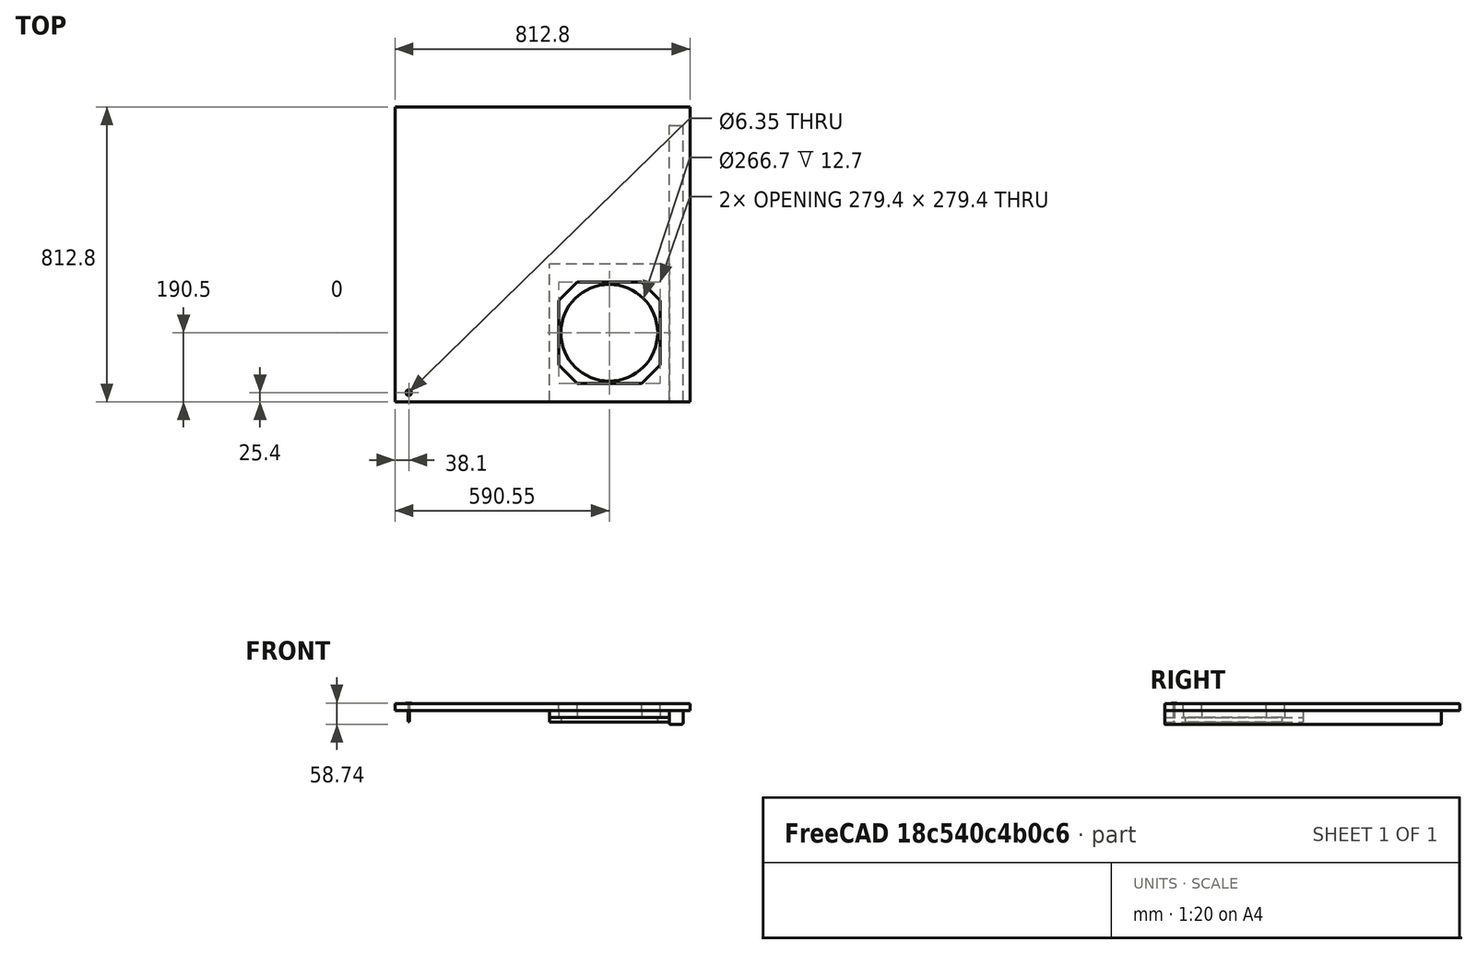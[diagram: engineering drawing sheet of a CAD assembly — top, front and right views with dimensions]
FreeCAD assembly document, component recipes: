
FREECAD ASSEMBLY — COMPONENT RECIPES ("Inlet_Wall")

This assembly document has 15 components, labeled P0..P14 below (a component is one placed body or linked part). 0 of them carry a construction recipe — the FreeCAD feature program that regenerates the part from scratch, quoted from this document or its linked companion documents; the rest are supplied as boundary geometry only. No exploded tour is included for this assembly.
COMPONENT P0 — geometry summary ("IF_A001"; no construction recipe available for this part):
  bounding box: 762.0 x 38.1 x 38.1 mm
  tessellated surface: 252 triangles
  volume: 1099533 mm^3 (99% of its bounding box)
  symmetry: 2-fold rotationally symmetric about the x axis; 4-fold rotationally symmetric about the y axis; 2-fold rotationally symmetric about the z axis; mirror-symmetric across its x mid-plane, z mid-plane
COMPONENT P1 — geometry summary ("Screw_w_Washer_B006"; no construction recipe available for this part):
  bounding box: 50.8 x 15.9 x 15.9 mm
  tessellated surface: 2,646 triangles
  volume: 650 mm^3 (5% of its bounding box)
  symmetry: 4-fold rotationally symmetric about the z axis; mirror-symmetric across its y mid-plane
COMPONENT P2 — geometry summary ("Screw_w_Washer_B007"; no construction recipe available for this part):
  bounding box: 50.8 x 15.9 x 15.9 mm
  tessellated surface: 2,646 triangles
  volume: 650 mm^3 (5% of its bounding box)
  symmetry: 4-fold rotationally symmetric about the z axis; mirror-symmetric across its y mid-plane
COMPONENT P3 — geometry summary ("Screw_w_Washer_B008"; no construction recipe available for this part):
  bounding box: 50.8 x 15.9 x 15.9 mm
  tessellated surface: 2,646 triangles
  volume: 650 mm^3 (5% of its bounding box)
  symmetry: 4-fold rotationally symmetric about the z axis; mirror-symmetric across its y mid-plane
COMPONENT P4 — geometry summary ("Screw_w_Washer_B009"; no construction recipe available for this part):
  bounding box: 50.8 x 15.9 x 15.9 mm
  tessellated surface: 2,646 triangles
  volume: 650 mm^3 (5% of its bounding box)
  symmetry: 4-fold rotationally symmetric about the z axis; mirror-symmetric across its y mid-plane
COMPONENT P5 — geometry summary ("Screw_w_Washer_B010"; no construction recipe available for this part):
  bounding box: 50.8 x 15.9 x 15.9 mm
  tessellated surface: 2,646 triangles
  volume: 650 mm^3 (5% of its bounding box)
  symmetry: 4-fold rotationally symmetric about the z axis; mirror-symmetric across its y mid-plane
COMPONENT P6 — geometry summary ("Screw_w_Washer_B011"; no construction recipe available for this part):
  bounding box: 50.8 x 15.9 x 15.9 mm
  tessellated surface: 2,646 triangles
  volume: 650 mm^3 (5% of its bounding box)
  symmetry: 4-fold rotationally symmetric about the z axis; mirror-symmetric across its y mid-plane
COMPONENT P7 — geometry summary ("Screw_w_Washer_B012"; no construction recipe available for this part):
  bounding box: 50.8 x 15.9 x 15.9 mm
  tessellated surface: 2,646 triangles
  volume: 650 mm^3 (5% of its bounding box)
  symmetry: 4-fold rotationally symmetric about the z axis; mirror-symmetric across its y mid-plane
COMPONENT P8 — geometry summary ("Screw_w_Washer_B013"; no construction recipe available for this part):
  bounding box: 50.8 x 15.9 x 15.9 mm
  tessellated surface: 2,646 triangles
  volume: 650 mm^3 (5% of its bounding box)
  symmetry: 4-fold rotationally symmetric about the z axis; mirror-symmetric across its y mid-plane
COMPONENT P9 — geometry summary ("Screw_w_Washer_B014"; no construction recipe available for this part):
  bounding box: 50.8 x 15.9 x 15.9 mm
  tessellated surface: 2,646 triangles
  volume: 650 mm^3 (5% of its bounding box)
  symmetry: 4-fold rotationally symmetric about the z axis; mirror-symmetric across its y mid-plane
COMPONENT P10 — geometry summary ("Screw_w_Washer_B015"; no construction recipe available for this part):
  bounding box: 50.8 x 15.9 x 15.9 mm
  tessellated surface: 2,646 triangles
  volume: 650 mm^3 (5% of its bounding box)
  symmetry: 4-fold rotationally symmetric about the z axis; mirror-symmetric across its y mid-plane
COMPONENT P11 — geometry summary ("Screw_w_Washer_B016"; no construction recipe available for this part):
  bounding box: 50.8 x 15.9 x 15.9 mm
  tessellated surface: 2,646 triangles
  volume: 650 mm^3 (5% of its bounding box)
  symmetry: 4-fold rotationally symmetric about the z axis; mirror-symmetric across its y mid-plane
COMPONENT P12 — geometry summary ("Screw_w_Washer_B017"; no construction recipe available for this part):
  bounding box: 50.8 x 15.9 x 15.9 mm
  tessellated surface: 2,646 triangles
  volume: 650 mm^3 (5% of its bounding box)
  symmetry: 4-fold rotationally symmetric about the z axis; mirror-symmetric across its y mid-plane
COMPONENT P13 — geometry summary ("Screw_w_Washer_B018"; no construction recipe available for this part):
  bounding box: 50.8 x 15.9 x 15.9 mm
  tessellated surface: 2,646 triangles
  volume: 650 mm^3 (5% of its bounding box)
  symmetry: 4-fold rotationally symmetric about the z axis; mirror-symmetric across its y mid-plane
COMPONENT P14 — geometry summary ("Screw_w_Washer_B019"; no construction recipe available for this part):
  bounding box: 50.8 x 15.9 x 15.9 mm
  tessellated surface: 2,646 triangles
  volume: 650 mm^3 (5% of its bounding box)
  symmetry: 4-fold rotationally symmetric about the z axis; mirror-symmetric across its y mid-plane
PROVENANCE & LICENSES
A FreeCAD (.FCStd) document from a public repository crawl; recipes are the document's own serialized feature recipes (and, for linked parts, companion documents' recipes).
License: gpl-3.0.
